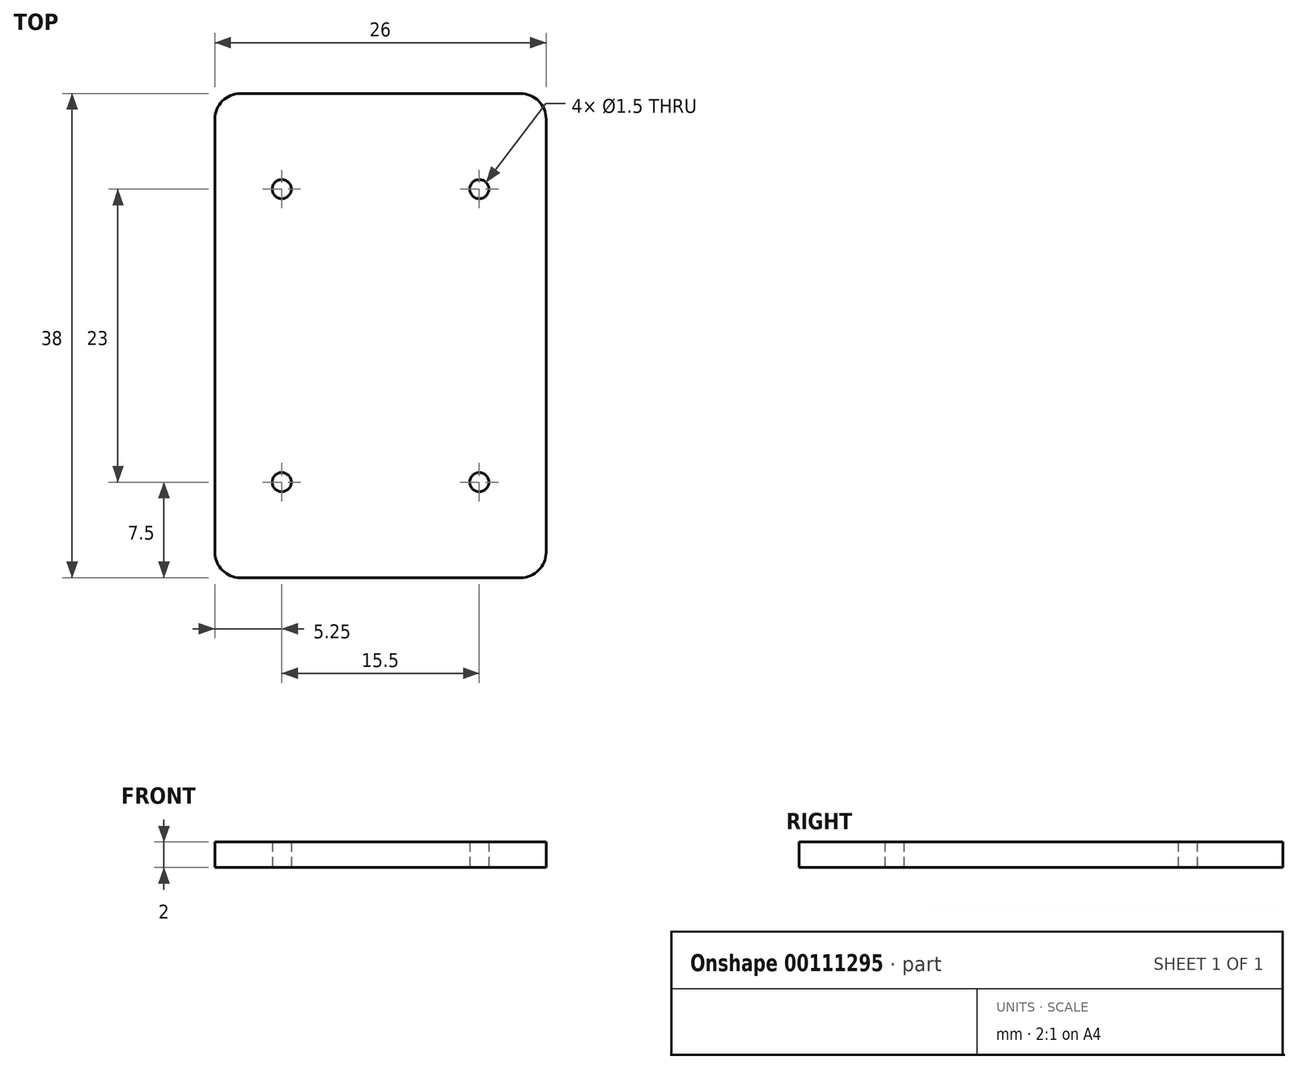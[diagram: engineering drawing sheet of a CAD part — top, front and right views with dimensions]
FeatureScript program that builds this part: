
annotation { "Feature Type Name" : "Feature", "Feature Type Description" : "" }
export const myFeature = defineFeature(function(context is Context, id is Id, definition is map)
    precondition{}
    {
        {
            var Q0;
            Q0=qCreatedBy(makeId("Top.planeOp"),FACE);
            var sketch = newSketch(context, id + "F0", { "sketchPlane" : qUnion([Q0])});
            skLineSegment(sketch, "E0.bottom", {"start": v(11, -19) * mm, "end": v(-11, -19) * mm});
            skLineSegment(sketch, "E0.top", {"start": v(11, 19) * mm, "end": v(-11, 19) * mm});
            skLineSegment(sketch, "E0.left", {"start": v(13, -17) * mm, "end": v(13, 17) * mm});
            skLineSegment(sketch, "E0.right", {"start": v(-13, -17) * mm, "end": v(-13, 17) * mm});
            skPoint(sketch, "E0.middle", {"position": v(0, 0) * mm});
            skPoint(sketch, "E1.visualSharp", {"position": v(-13, 19) * mm});
            skArc(sketch, "E1.filletArc", {"start": v(-11, 19) * mm, "mid": v(-12.41, 18.41) * mm, "end": v(-13, 17) * mm});
            skPoint(sketch, "E2.visualSharp", {"position": v(13, 19) * mm});
            skArc(sketch, "E2.filletArc", {"start": v(13, 17) * mm, "mid": v(12.41, 18.41) * mm, "end": v(11, 19) * mm});
            skPoint(sketch, "E3.visualSharp", {"position": v(13, -19) * mm});
            skArc(sketch, "E3.filletArc", {"start": v(11, -19) * mm, "mid": v(12.41, -18.41) * mm, "end": v(13, -17) * mm});
            skPoint(sketch, "E4.visualSharp", {"position": v(-13, -19) * mm});
            skArc(sketch, "E4.filletArc", {"start": v(-13, -17) * mm, "mid": v(-12.41, -18.41) * mm, "end": v(-11, -19) * mm});
            skLineSegment(sketch, "E5.bottom", {"start": v(7.75, -11.5) * mm, "end": v(-7.75, -11.5) * mm, "construction": true});
            skLineSegment(sketch, "E5.top", {"start": v(7.75, 11.5) * mm, "end": v(-7.75, 11.5) * mm, "construction": true});
            skLineSegment(sketch, "E5.left", {"start": v(7.75, -11.5) * mm, "end": v(7.75, 11.5) * mm, "construction": true});
            skLineSegment(sketch, "E5.right", {"start": v(-7.75, -11.5) * mm, "end": v(-7.75, 11.5) * mm, "construction": true});
            skCircle(sketch, "E6", {"center": v(-7.75, 11.5) * mm, "radius": 0.75 * mm});
            skCircle(sketch, "E7", {"center": v(7.75, 11.5) * mm, "radius": 0.75 * mm});
            skCircle(sketch, "E8", {"center": v(-7.75, -11.5) * mm, "radius": 0.75 * mm});
            skCircle(sketch, "E9", {"center": v(7.75, -11.5) * mm, "radius": 0.75 * mm});
            skSolve(sketch);
        }
        {
            var Q0;
            Q0 = qSketchRegion(id + "F0", true);
            extrude(context, id + "F1", {"entities" : qUnion([Q0]), "depth" : 2 * mm});
        }
    });
